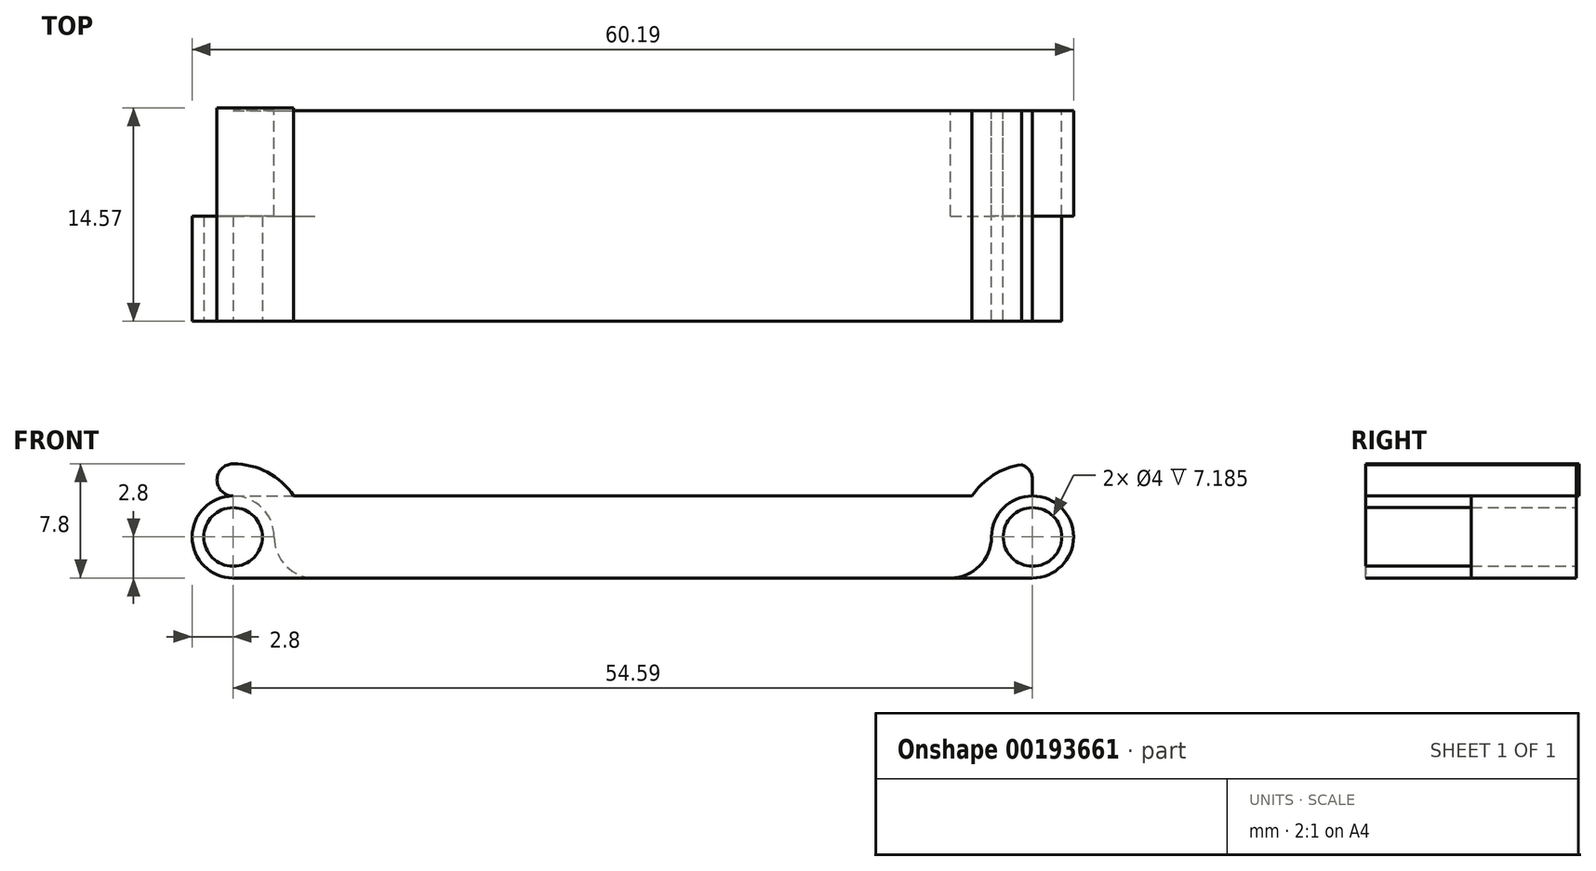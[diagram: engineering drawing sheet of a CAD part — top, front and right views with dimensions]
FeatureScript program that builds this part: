
annotation { "Feature Type Name" : "Feature", "Feature Type Description" : "" }
export const myFeature = defineFeature(function(context is Context, id is Id, definition is map)
    precondition{}
    {
        {
            var Q0;
            Q0=qCreatedBy(makeId("Front.planeOp"),FACE);
            var sketch = newSketch(context, id + "F0", { "sketchPlane" : qUnion([Q0])});
            skLineSegment(sketch, "E0.bottom", {"start": v(0, 0) * mm, "end": v(57.39, 0) * mm});
            skLineSegment(sketch, "E0.top", {"start": v(0, 5.6) * mm, "end": v(53.25, 5.6) * mm});
            skLineSegment(sketch, "E0.left", {"start": v(0, 0) * mm, "end": v(0, 5.6) * mm});
            skLineSegment(sketch, "E1", {"start": v(60.19, 2.8) * mm, "end": v(54.59, 2.8) * mm, "construction": true});
            skPoint(sketch, "E1.endSnap0", {"position": v(60.19, 2.8) * mm});
            skLineSegment(sketch, "E2", {"start": v(57.4, 2.8) * mm, "end": v(60.2, 0) * mm, "construction": true});
            skCircle(sketch, "E3", {"center": v(57.39, 2.8) * mm, "radius": 2 * mm});
            skArc(sketch, "E4", {"start": v(57.39, 0) * mm, "mid": v(59.37, 4.78) * mm, "end": v(54.59, 2.8) * mm});
            skArc(sketch, "E5", {"start": v(56.64, 7.74) * mm, "mid": v(54.72, 7.03) * mm, "end": v(53.25, 5.6) * mm});
            skLineSegment(sketch, "E6", {"start": v(57.39, 2.8) * mm, "end": v(57.39, 7.8) * mm, "construction": true});
            skLineSegment(sketch, "E7", {"start": v(57.39, 6.7) * mm, "end": v(57.39, 5.6) * mm, "construction": true});
            skArc(sketch, "E8", {"start": v(57.39, 5.6) * mm, "mid": v(57.67, 7.76) * mm, "end": v(56.84, 5.75) * mm, "construction": true});
            skLineSegment(sketch, "E9", {"start": v(57.39, 6.7) * mm, "end": v(58.49, 6.7) * mm, "construction": true});
            skLineSegment(sketch, "E10", {"start": v(57.39, 6.7) * mm, "end": v(56.29, 6.7) * mm, "construction": true});
            skLineSegment(sketch, "E11", {"start": v(55.45, 7.4) * mm, "end": v(55.45, 7.4) * mm});
            skPoint(sketch, "E12.orphan", {"position": v(60.19, 5.6) * mm});
            skLineSegment(sketch, "E13", {"start": v(57.39, 6.7) * mm, "end": v(57.39, 5.6) * mm});
            skArc(sketch, "E14.trimOffspring", {"start": v(57.39, 6.7) * mm, "mid": v(57.18, 7.34) * mm, "end": v(56.64, 7.74) * mm});
            skCircle(sketch, "E15", {"center": v(54.59, 2.8) * mm, "radius": 2.8 * mm, "construction": true});
            skArc(sketch, "E16", {"start": v(51.8, 0) * mm, "mid": v(53.77, 0.82) * mm, "end": v(54.59, 2.8) * mm});
            skSolve(sketch);
        }
        {
            var Q0;
            Q0=makeQuery(id+"F0.imprint","IMPRINT",FACE,{"disambiguationData":[TD([[makeQuery(id+"F0.imprint","IMPRINT",EDGE,{"derivedFrom":sQuery(id+"F0.wireOp",EDGE,"E0.top")}),-1.0]])]});
            var Q1;
            Q1=makeQuery(id+"F0.imprint","IMPRINT",FACE,{"disambiguationData":[TD([[makeQuery(id+"F0.imprint","IMPRINT",EDGE,{"derivedFrom":sQuery(id+"F0.wireOp",EDGE,"E3")}),1.0]])]});
            extrude(context, id + "F1", {"entities" : qUnion([Q0, Q1]), "depth" : 14.37 * mm});
        }
        {
            var Q0;
            Q0=makeQuery(id+"F0.imprint","IMPRINT",FACE,{"disambiguationData":[TD([[makeQuery(id+"F0.imprint","IMPRINT",EDGE,{"derivedFrom":sQuery(id+"F0.wireOp",EDGE,"E3")}),-1.0]])]});
            extrude(context, id + "F2", {"entities" : qUnion([Q0]), "depth" : 7.18 * mm});
        }
        {
            var Q0;
            Q0=makeQuery(id+"F1.opExtrude","CAP_FACE",FACE,{"disambiguationData":[OSD([sQuery(id+"F0.wireOp",EDGE,"E0.bottom"),sQuery(id+"F0.wireOp",EDGE,"E0.top"),sQuery(id+"F0.wireOp",EDGE,"E0.left"),sQuery(id+"F0.wireOp",EDGE,"E4"),sQuery(id+"F0.wireOp",EDGE,"E5"),sQuery(id+"F0.wireOp",EDGE,"E13"),sQuery(id+"F0.wireOp",EDGE,"E14.trimOffspring"),sQuery(id+"F0.wireOp",EDGE,"E16")])],"isStart":false});
            var sketch = newSketch(context, id + "F3", { "sketchPlane" : qUnion([Q0])});
            skLineSegment(sketch, "E17", {"start": v(0, 5.6) * mm, "end": v(0, 0) * mm, "construction": true});
            skLineSegment(sketch, "E18", {"start": v(0, 2.8) * mm, "end": v(5.6, 2.8) * mm, "construction": true});
            skCircle(sketch, "E19", {"center": v(2.8, 2.8) * mm, "radius": 2 * mm});
            skCircle(sketch, "E20", {"center": v(2.8, 2.8) * mm, "radius": 2.8 * mm});
            skArc(sketch, "E21", {"start": v(6.94, 0) * mm, "mid": v(7.22, 5.15) * mm, "end": v(2.8, 7.8) * mm});
            skCircle(sketch, "E22", {"center": v(5.6, 2.8) * mm, "radius": 2.8 * mm, "construction": true});
            skCircle(sketch, "E23", {"center": v(8.4, 2.8) * mm, "radius": 2.8 * mm});
            skLineSegment(sketch, "E24", {"start": v(2.8, 5.6) * mm, "end": v(2.8, 7.8) * mm, "construction": true});
            skLineSegment(sketch, "E25.bottom", {"start": v(6.94, 0) * mm, "end": v(0, 0) * mm});
            skLineSegment(sketch, "E25.top", {"start": v(6.94, 5.6) * mm, "end": v(0, 5.6) * mm});
            skLineSegment(sketch, "E25.left", {"start": v(6.94, 0) * mm, "end": v(6.94, 5.6) * mm});
            skLineSegment(sketch, "E25.right", {"start": v(0, 0) * mm, "end": v(0, 5.6) * mm});
            skCircle(sketch, "E26", {"center": v(2.8, 6.7) * mm, "radius": 1.1 * mm});
            skSolve(sketch);
        }
        {
            var Q0;
            {var subQ0=sQuery(id+"F3.wireOp",EDGE,"E26");var subQ1=makeQuery(id+"F3.imprint","INTERSECT",VERTEX,{"derivedFrom":[sQuery(id+"F3.wireOp",EDGE,"E21"),subQ0]});Q0=makeQuery(id+"F3.imprint","IMPRINT",FACE,{"disambiguationData":[TD([[makeQuery(id+"F3.imprint","IMPRINT",EDGE,{"disambiguationData":[TD([[subQ1,-1.0]])],"derivedFrom":subQ0}),1.0]])]});}
            var Q1;
            {var subQ0=sQuery(id+"F3.wireOp",EDGE,"E26");var subQ1=sQuery(id+"F3.wireOp",EDGE,"E21");var subQ2=makeQuery(id+"F3.imprint","INTERSECT",VERTEX,{"derivedFrom":[subQ1,subQ0]});Q1=makeQuery(id+"F3.imprint","IMPRINT",FACE,{"disambiguationData":[TD([[makeQuery(id+"F3.imprint","IMPRINT",EDGE,{"disambiguationData":[TD([[subQ2,1.0]])],"derivedFrom":subQ0}),-1.0]])]});}
            extrude(context, id + "F4", {"entities" : qUnion([Q0, Q1]), "operationType" : NewBodyOperationType.ADD, "oppositeDirection" : true, "depth" : 14.57 * mm});
        }
        {
            var Q0;
            {var subQ0=sQuery(id+"F3.wireOp",EDGE,"E25.right");var subQ3=sQuery(id+"F3.wireOp",EDGE,"E25.top");var subQ5=makeQuery(id+"F3.imprint","INTERSECT",VERTEX,{"derivedFrom":[subQ3,subQ0]});Q0=makeQuery(id+"F3.imprint","IMPRINT",FACE,{"disambiguationData":[TD([[makeQuery(id+"F3.imprint","IMPRINT",EDGE,{"disambiguationData":[TD([[subQ5,1.0]])],"derivedFrom":subQ0}),-1.0]])]});}
            var Q1;
            {var subQ0=sQuery(id+"F3.wireOp",EDGE,"E25.right");var subQ1=sQuery(id+"F3.wireOp",EDGE,"E20");var subQ2=makeQuery(id+"F3.imprint","INTERSECT",VERTEX,{"derivedFrom":[subQ1,subQ0]});Q1=makeQuery(id+"F3.imprint","IMPRINT",FACE,{"disambiguationData":[TD([[makeQuery(id+"F3.imprint","IMPRINT",EDGE,{"disambiguationData":[TD([[subQ2,-1.0]])],"derivedFrom":subQ1}),-1.0]])]});}
            var Q2;
            Q2=makeQuery(id+"F3.imprint","IMPRINT",FACE,{"disambiguationData":[TD([[makeQuery(id+"F3.imprint","IMPRINT",EDGE,{"derivedFrom":sQuery(id+"F3.wireOp",EDGE,"E19")}),1.0]])]});
            extrude(context, id + "F5", {"entities" : qUnion([Q0, Q1, Q2]), "operationType" : NewBodyOperationType.REMOVE, "oppositeDirection" : true, "depth" : 14.37 * mm});
        }
        {
            var Q0;
            Q0=makeQuery(id+"F0.imprint","IMPRINT",FACE,{"disambiguationData":[TD([[makeQuery(id+"F0.imprint","IMPRINT",EDGE,{"derivedFrom":sQuery(id+"F0.wireOp",EDGE,"E0.top")}),-1.0]])]});
            var sketch = newSketch(context, id + "F6", { "sketchPlane" : qUnion([Q0])});
            skLineSegment(sketch, "E27.bottom", {"start": v(0, 0) * mm, "end": v(5.6, 0) * mm, "construction": true});
            skLineSegment(sketch, "E27.top", {"start": v(0, 5.6) * mm, "end": v(5.6, 5.6) * mm, "construction": true});
            skLineSegment(sketch, "E27.left", {"start": v(0, 0) * mm, "end": v(0, 5.6) * mm, "construction": true});
            skLineSegment(sketch, "E27.right", {"start": v(5.6, 0) * mm, "end": v(5.6, 5.6) * mm, "construction": true});
            skLineSegment(sketch, "E28", {"start": v(5.6, 2.8) * mm, "end": v(0, 2.8) * mm, "construction": true});
            skArc(sketch, "E29", {"start": v(5.6, 2.8) * mm, "mid": v(0.82, 4.78) * mm, "end": v(2.8, 0) * mm});
            skLineSegment(sketch, "E30", {"start": v(5.6, 2.8) * mm, "end": v(5.6, 0) * mm});
            skLineSegment(sketch, "E31", {"start": v(5.6, 0) * mm, "end": v(2.8, 0) * mm});
            skCircle(sketch, "E32", {"center": v(5.6, 2.8) * mm, "radius": 2.8 * mm, "construction": true});
            skArc(sketch, "E33", {"start": v(5.6, 2.8) * mm, "mid": v(6.42, 0.82) * mm, "end": v(8.4, 0) * mm});
            skLineSegment(sketch, "E34", {"start": v(8.4, 0) * mm, "end": v(2.8, 0) * mm});
            skLineSegment(sketch, "E35", {"start": v(8.4, 0) * mm, "end": v(5.6, 0) * mm});
            skSolve(sketch);
        }
        {
            var Q0;
            Q0 = qSketchRegion(id + "F6", true);
            extrude(context, id + "F7", {"entities" : qUnion([Q0]), "operationType" : NewBodyOperationType.REMOVE, "depth" : 7.18 * mm});
        }
    });
